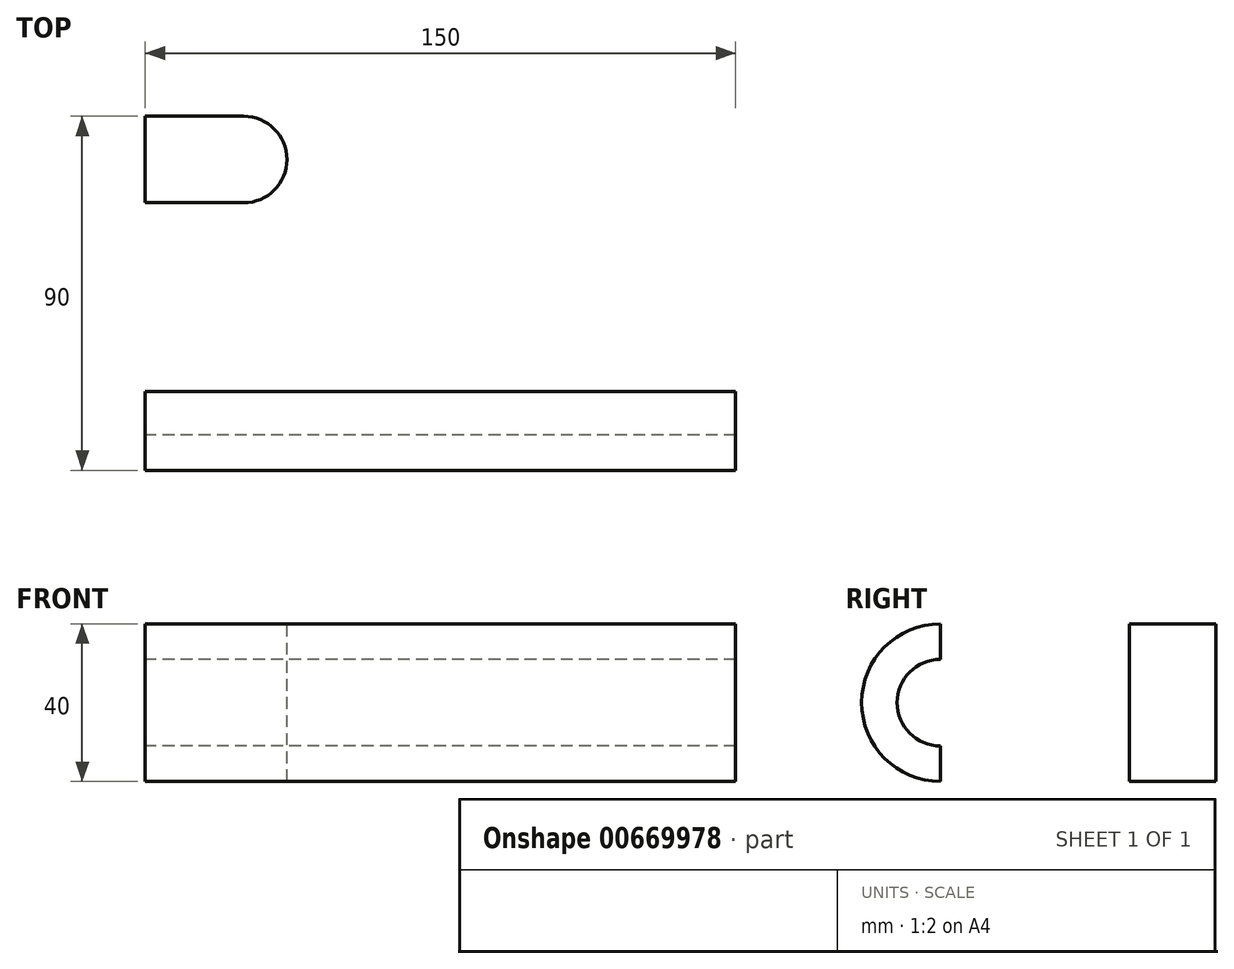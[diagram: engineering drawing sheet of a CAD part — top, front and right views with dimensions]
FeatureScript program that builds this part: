
annotation { "Feature Type Name" : "Feature", "Feature Type Description" : "" }
export const myFeature = defineFeature(function(context is Context, id is Id, definition is map)
    precondition{}
    {
        {
            var Q0;
            Q0=qCreatedBy(makeId("Right.planeOp"),FACE);
            var sketch = newSketch(context, id + "F0", { "sketchPlane" : qUnion([Q0])});
            skLineSegment(sketch, "E0.bottom", {"start": v(-44, 40) * mm, "end": v(44, 40) * mm});
            skLineSegment(sketch, "E0.top", {"start": v(-44, 0) * mm, "end": v(44, 0) * mm});
            skLineSegment(sketch, "E0.right", {"start": v(44, 40) * mm, "end": v(44, 0) * mm});
            skArc(sketch, "E1", {"start": v(-44, 40) * mm, "mid": v(-64, 20) * mm, "end": v(-44, 0) * mm});
            skCircle(sketch, "E2", {"center": v(-44, 20) * mm, "radius": 11 * mm});
            skSolve(sketch);
        }
        {
            var Q0;
            Q0=makeQuery(id+"F0.imprint","IMPRINT",FACE,{"disambiguationData":[TD([[makeQuery(id+"F0.imprint","IMPRINT",EDGE,{"derivedFrom":sQuery(id+"F0.wireOp",EDGE,"E0.bottom")}),-1.0]])]});
            extrude(context, id + "F1", {"entities" : qUnion([Q0]), "depth" : 150 * mm, "offsetDistance" : 25 * mm});
        }
        {
            var Q0;
            Q0=makeQuery(id+"F1.opExtrude","SWEPT_FACE",FACE,{"disambiguationData":[OSD([sQuery(id+"F0.wireOp",EDGE,"E0.bottom")])]});
            var sketch = newSketch(context, id + "F2", { "sketchPlane" : qUnion([Q0])});
            skLineSegment(sketch, "E3", {"start": v(150, 26) * mm, "end": v(125, 26) * mm});
            skLineSegment(sketch, "E4", {"start": v(125, 4) * mm, "end": v(150, 4) * mm});
            skArc(sketch, "E5", {"start": v(125, 26) * mm, "mid": v(114, 15) * mm, "end": v(125, 4) * mm});
            skLineSegment(sketch, "E6", {"start": v(75, 44) * mm, "end": v(75, -44) * mm, "construction": true});
            skLineSegment(sketch, "E7.MirrorCS", {"start": v(25, 4) * mm, "end": v(0, 4) * mm});
            skLineSegment(sketch, "E8.MirrorCS", {"start": v(0, 26) * mm, "end": v(25, 26) * mm});
            skArc(sketch, "E9.MirrorCS", {"start": v(25, 26) * mm, "mid": v(36, 15) * mm, "end": v(25, 4) * mm});
            skSolve(sketch);
        }
        {
            var Q0;
            {var subQ0=sQuery(id+"F2.wireOp",EDGE,"E3");Q0=makeQuery(id+"F2.imprint","IMPRINT",FACE,{"disambiguationData":[TD([[makeQuery(id+"F2.imprint","IMPRINT",EDGE,{"derivedFrom":subQ0}),1.0]])]});}
            var Q1;
            Q1=makeQuery(id+"F2.imprint","IMPRINT",FACE,{"disambiguationData":[TD([[makeQuery(id+"F2.imprint","IMPRINT",EDGE,{"derivedFrom":sQuery(id+"F2.wireOp",EDGE,"E9.MirrorCS")}),-1.0]])]});
            extrude(context, id + "F3", {"entities" : qUnion([Q0, Q1]), "operationType" : NewBodyOperationType.REMOVE, "oppositeDirection" : true, "depth" : 50 * mm, "offsetDistance" : 25 * mm});
        }
    });
